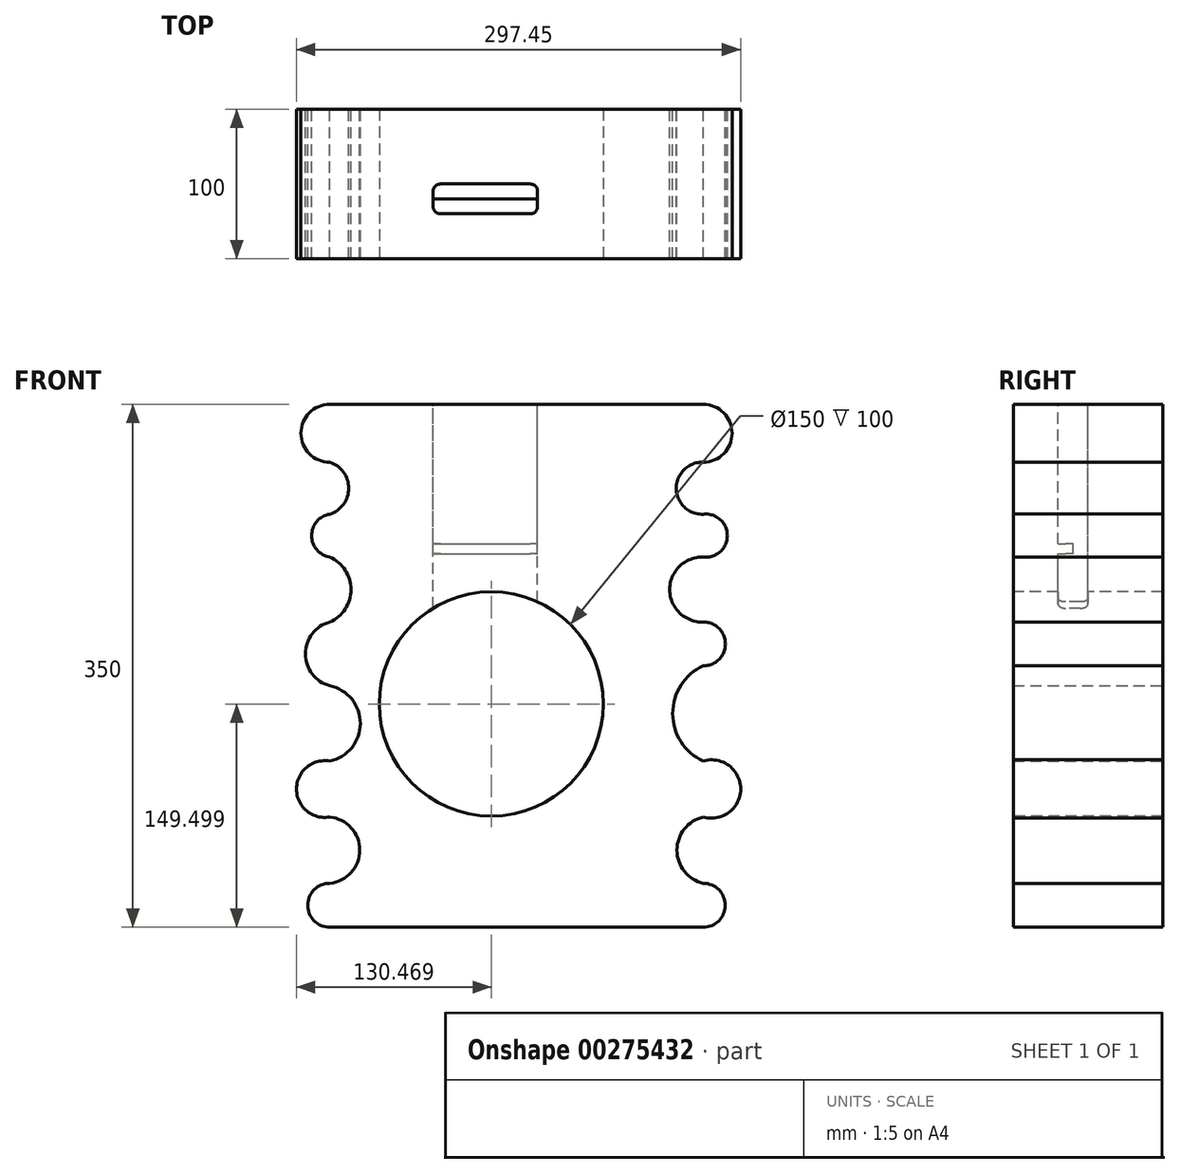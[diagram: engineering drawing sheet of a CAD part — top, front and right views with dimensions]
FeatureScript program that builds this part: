
annotation { "Feature Type Name" : "Feature", "Feature Type Description" : "" }
export const myFeature = defineFeature(function(context is Context, id is Id, definition is map)
    precondition{}
    {
        {
            var Q0;
            Q0=qCreatedBy(makeId("Front.planeOp"),FACE);
            var sketch = newSketch(context, id + "F0", { "sketchPlane" : qUnion([Q0])});
            skLineSegment(sketch, "E0.bottom", {"start": v(-75, 175) * mm, "end": v(175, 175) * mm});
            skLineSegment(sketch, "E0.top", {"start": v(-75, -175) * mm, "end": v(175, -175) * mm});
            skArc(sketch, "E1", {"start": v(-75, 175) * mm, "mid": v(-94.37, 155.63) * mm, "end": v(-75, 136.27) * mm});
            skArc(sketch, "E2", {"start": v(-75, 101.48) * mm, "mid": v(-62.33, 118.87) * mm, "end": v(-75, 136.27) * mm});
            skArc(sketch, "E3", {"start": v(-75, 101.48) * mm, "mid": v(-87.22, 87.13) * mm, "end": v(-75, 72.78) * mm});
            skArc(sketch, "E4", {"start": v(-75, 29.3) * mm, "mid": v(-60.87, 51.04) * mm, "end": v(-75, 72.78) * mm});
            skArc(sketch, "E5", {"start": v(-75, 29.3) * mm, "mid": v(-91.3, 7.98) * mm, "end": v(-75, -13.32) * mm});
            skArc(sketch, "E6", {"start": v(-75, -63.77) * mm, "mid": v(-54.56, -38.55) * mm, "end": v(-75, -13.32) * mm});
            skArc(sketch, "E7", {"start": v(-75, -63.77) * mm, "mid": v(-97.32, -82.47) * mm, "end": v(-75, -101.17) * mm});
            skArc(sketch, "E8", {"start": v(-75, -145.52) * mm, "mid": v(-54.98, -123.35) * mm, "end": v(-75, -101.17) * mm});
            skArc(sketch, "E9", {"start": v(-75, -145.52) * mm, "mid": v(-89.74, -160.26) * mm, "end": v(-75, -175) * mm});
            skArc(sketch, "E10", {"start": v(175, 136.27) * mm, "mid": v(194.37, 155.63) * mm, "end": v(175, 175) * mm});
            skArc(sketch, "E11", {"start": v(175, 136.27) * mm, "mid": v(156.97, 118.87) * mm, "end": v(175, 101.48) * mm});
            skArc(sketch, "E12", {"start": v(175, 72.78) * mm, "mid": v(191.15, 87.13) * mm, "end": v(175, 101.48) * mm});
            skArc(sketch, "E13", {"start": v(175, 72.78) * mm, "mid": v(152.58, 51.04) * mm, "end": v(175, 29.3) * mm});
            skArc(sketch, "E14", {"start": v(175, 0) * mm, "mid": v(189.87, 14.65) * mm, "end": v(175, 29.3) * mm});
            skArc(sketch, "E15", {"start": v(175, 0) * mm, "mid": v(154.58, -31.88) * mm, "end": v(175, -63.77) * mm});
            skArc(sketch, "E16", {"start": v(175, -101.17) * mm, "mid": v(200.13, -82.47) * mm, "end": v(175, -63.77) * mm});
            skArc(sketch, "E17", {"start": v(175, -101.17) * mm, "mid": v(157.45, -123.35) * mm, "end": v(175, -145.52) * mm});
            skArc(sketch, "E18", {"start": v(175, -175) * mm, "mid": v(189.74, -160.26) * mm, "end": v(175, -145.52) * mm});
            skSolve(sketch);
        }
        {
            var Q0;
            Q0=qSketchRegion(id+"F0",true);
            extrude(context, id + "F1", {"entities" : qUnion([Q0]), "depth" : 100 * mm});
        }
        {
            var Q0;
            Q0=makeQuery(id+"F1.opExtrude","CAP_FACE",FACE,{"disambiguationData":[OSD([sQuery(id+"F0.wireOp",EDGE,"E0.bottom"),sQuery(id+"F0.wireOp",EDGE,"E0.top"),sQuery(id+"F0.wireOp",EDGE,"E0.left"),sQuery(id+"F0.wireOp",EDGE,"E0.right")])],"isStart":false});
            var sketch = newSketch(context, id + "F2", { "sketchPlane" : qUnion([Q0])});
            skCircle(sketch, "E19", {"center": v(33.15, -25.5) * mm, "radius": 75 * mm});
            skSolve(sketch);
        }
        {
            var Q0;
            Q0=makeQuery(id+"F1.opExtrude","SWEPT_FACE",FACE,{"disambiguationData":[OSD([sQuery(id+"F0.wireOp",EDGE,"E0.bottom")])]});
            var sketch = newSketch(context, id + "F3", { "sketchPlane" : qUnion([Q0])});
            skLineSegment(sketch, "E20.bottom", {"start": v(-0.88, -50) * mm, "end": v(59.12, -50) * mm});
            skLineSegment(sketch, "E20.top", {"start": v(-0.88, -70) * mm, "end": v(59.12, -70) * mm});
            skLineSegment(sketch, "E20.left", {"start": v(-5.88, -55) * mm, "end": v(-5.88, -65) * mm});
            skLineSegment(sketch, "E20.right", {"start": v(64.12, -55) * mm, "end": v(64.12, -65) * mm});
            skPoint(sketch, "E21.visualSharp", {"position": v(-5.88, -50) * mm});
            skArc(sketch, "E21.filletArc", {"start": v(-0.88, -50) * mm, "mid": v(-4.41, -51.46) * mm, "end": v(-5.88, -55) * mm});
            skPoint(sketch, "E22.visualSharp", {"position": v(64.12, -50) * mm});
            skArc(sketch, "E22.filletArc", {"start": v(64.12, -55) * mm, "mid": v(62.66, -51.46) * mm, "end": v(59.12, -50) * mm});
            skPoint(sketch, "E23.visualSharp", {"position": v(64.12, -70) * mm});
            skArc(sketch, "E23.filletArc", {"start": v(59.12, -70) * mm, "mid": v(62.66, -68.54) * mm, "end": v(64.12, -65) * mm});
            skPoint(sketch, "E24.visualSharp", {"position": v(-5.88, -70) * mm});
            skArc(sketch, "E24.filletArc", {"start": v(-5.88, -65) * mm, "mid": v(-4.41, -68.54) * mm, "end": v(-0.88, -70) * mm});
            skSolve(sketch);
        }
        {
            var Q0;
            Q0=qSketchRegion(id+"F3",true);
            extrude(context, id + "F4", {"entities" : qUnion([Q0]), "operationType" : NewBodyOperationType.REMOVE, "oppositeDirection" : true, "depth" : 145 * mm});
        }
        {
            var Q0;
            Q0=makeQuery(id+"F1.opExtrude","CAP_FACE",FACE,{"disambiguationData":[OSD([sQuery(id+"F0.wireOp",EDGE,"E0.bottom"),sQuery(id+"F0.wireOp",EDGE,"E0.top"),sQuery(id+"F0.wireOp",EDGE,"03f8dbdd-d0c8-423f-a74c-b74725071d69"),sQuery(id+"F0.wireOp",EDGE,"425002b4-c618-4dc9-981f-20556754a608")])],"isStart":false});
            var sketch = newSketch(context, id + "F5", { "sketchPlane" : qUnion([Q0])});
            skLineSegment(sketch, "E25.bottom", {"start": v(-59.42, 81.6) * mm, "end": v(69.62, 81.6) * mm});
            skLineSegment(sketch, "E25.top", {"start": v(-59.42, 74.95) * mm, "end": v(69.62, 74.95) * mm});
            skLineSegment(sketch, "E25.left", {"start": v(-59.42, 81.6) * mm, "end": v(-59.42, 74.95) * mm});
            skLineSegment(sketch, "E25.right", {"start": v(69.62, 81.6) * mm, "end": v(69.62, 74.95) * mm});
            skSolve(sketch);
        }
        {
            var Q0;
            Q0 = qSketchRegion(id + "F5", true);
            extrude(context, id + "F6", {"entities" : qUnion([Q0]), "operationType" : NewBodyOperationType.ADD, "oppositeDirection" : true, "depth" : 40 * mm});
        }
        {
            var Q0;
            Q0 = qSketchRegion(id + "F2", true);
            extrude(context, id + "F7", {"entities" : qUnion([Q0]), "operationType" : NewBodyOperationType.REMOVE, "oppositeDirection" : true, "depth" : 319 * mm});
        }
    });
